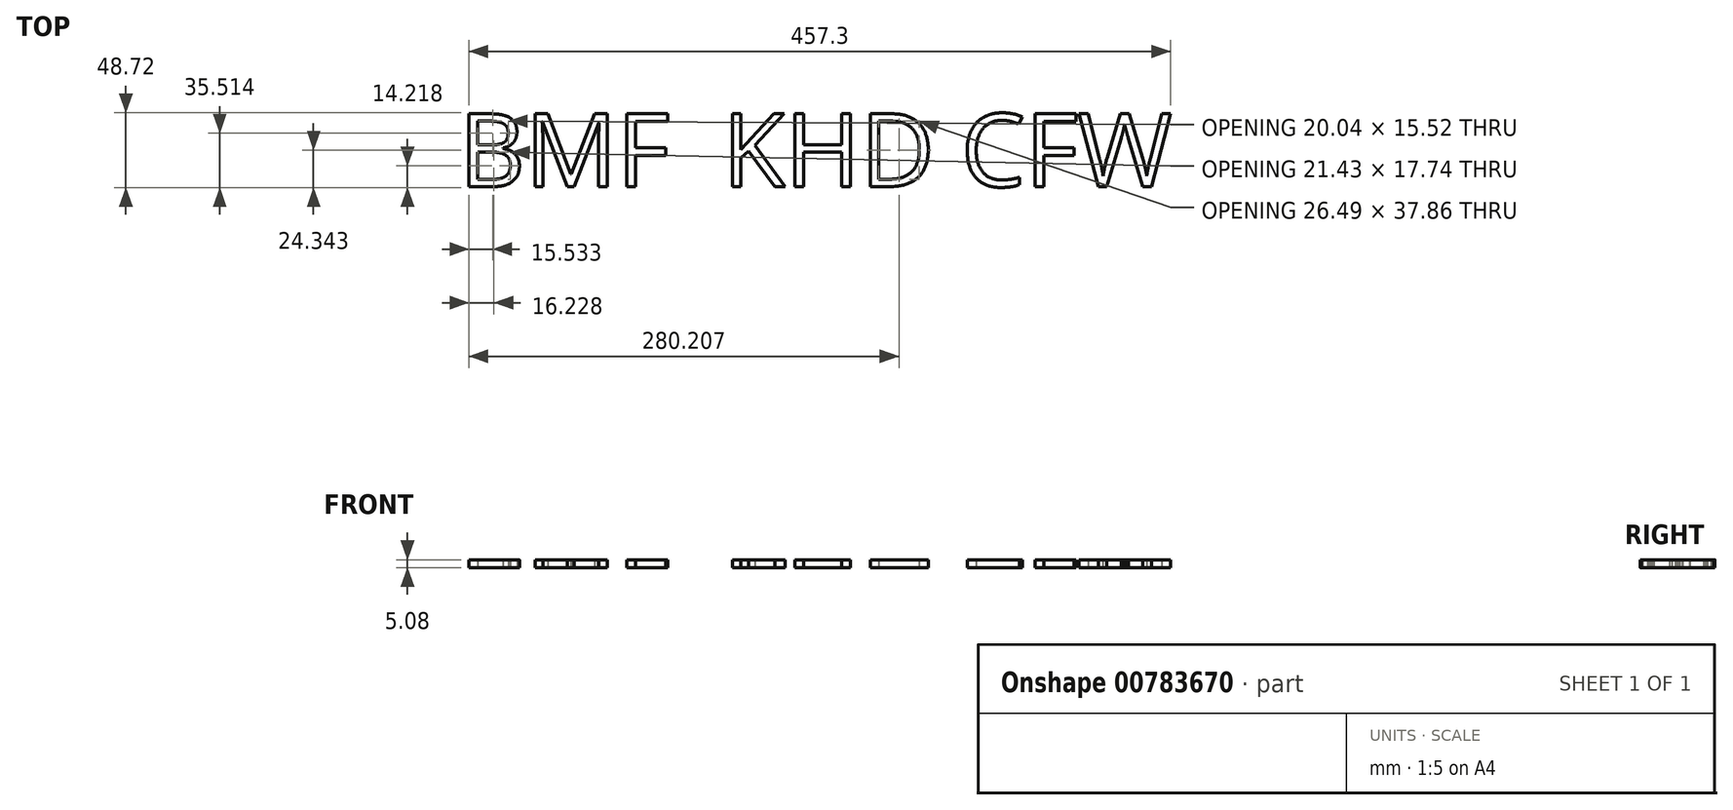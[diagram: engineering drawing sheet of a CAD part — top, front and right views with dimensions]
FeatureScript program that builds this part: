
annotation { "Feature Type Name" : "Feature", "Feature Type Description" : "" }
export const myFeature = defineFeature(function(context is Context, id is Id, definition is map)
    precondition{}
    {
        {
            var Q0;
            Q0=qCreatedBy(makeId("Top.planeOp"),FACE);
            var sketch = newSketch(context, id + "F0", { "sketchPlane" : qUnion([Q0])});
            skText(sketch, "E0", { "text": "BMF  KHD CFW ", "fontName": "OpenSans-Regular.ttf"});
            const initialGuessF0  = {"E0": [-0.2621, -0.0267, 1, 0, 0.0478]};
            skSetInitialGuess(sketch, initialGuessF0);
            skSolve(sketch);
        }
        {
            var Q0;
            Q0 = qSketchRegion(id + "F0", true);
            extrude(context, id + "F1", {"entities" : qUnion([Q0]), "depth" : 5.08 * mm, "offsetDistance" : 25.4 * mm});
        }
    });
